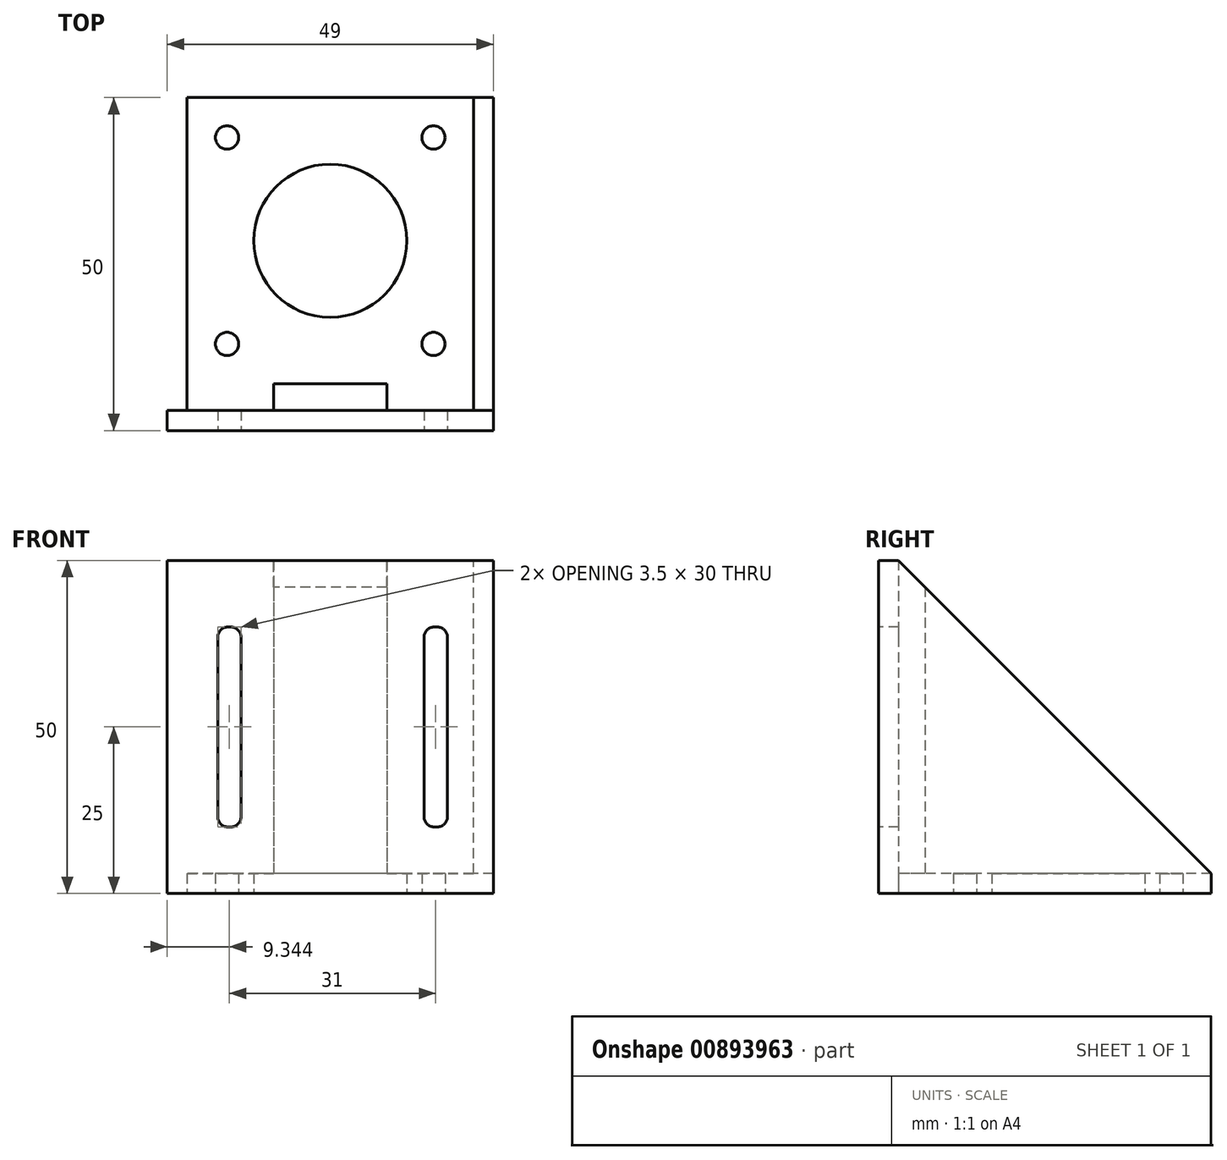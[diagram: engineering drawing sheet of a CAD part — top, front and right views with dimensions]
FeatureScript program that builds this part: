
annotation { "Feature Type Name" : "Feature", "Feature Type Description" : "" }
export const myFeature = defineFeature(function(context is Context, id is Id, definition is map)
    precondition{}
    {
        {
            var Q0;
            Q0=qCreatedBy(makeId("Top.planeOp"),FACE);
            var sketch = newSketch(context, id + "F0", { "sketchPlane" : qUnion([Q0])});
            skLineSegment(sketch, "E0.bottom", {"start": v(21.5, 21.5) * mm, "end": v(-21.5, 21.5) * mm});
            skLineSegment(sketch, "E0.top", {"start": v(21.5, -21.5) * mm, "end": v(-21.5, -21.5) * mm});
            skLineSegment(sketch, "E0.left", {"start": v(21.5, 21.5) * mm, "end": v(21.5, -21.5) * mm});
            skLineSegment(sketch, "E0.right", {"start": v(-21.5, 21.5) * mm, "end": v(-21.5, -21.5) * mm});
            skPoint(sketch, "E0.middle", {"position": v(0, 0) * mm});
            skCircle(sketch, "E1", {"center": v(0, 0) * mm, "radius": 11.5 * mm});
            skCircle(sketch, "E2", {"center": v(15.5, 15.5) * mm, "radius": 1.75 * mm});
            skCircle(sketch, "E3.0.1.0", {"center": v(15.5, -15.5) * mm, "radius": 1.75 * mm});
            skCircle(sketch, "E3.1.0.0", {"center": v(-15.5, 15.5) * mm, "radius": 1.75 * mm});
            skCircle(sketch, "E3.1.1.0", {"center": v(-15.5, -15.5) * mm, "radius": 1.75 * mm});
            skLineSegment(sketch, "E3.direction1", {"start": v(15.5, 15.5) * mm, "end": v(-15.5, 15.5) * mm, "construction": true});
            skLineSegment(sketch, "E3.direction2", {"start": v(15.5, 15.5) * mm, "end": v(15.5, -15.5) * mm, "construction": true});
            skLineSegment(sketch, "E4.top", {"start": v(-24.5, -28.5) * mm, "end": v(24.5, -28.5) * mm});
            skLineSegment(sketch, "E5.top", {"start": v(-24.5, -25.5) * mm, "end": v(24.5, -25.5) * mm});
            skLineSegment(sketch, "E5.left", {"start": v(-24.5, -28.5) * mm, "end": v(-24.5, -25.5) * mm});
            skLineSegment(sketch, "E5.right", {"start": v(24.5, -28.5) * mm, "end": v(24.5, -25.5) * mm});
            skLineSegment(sketch, "E6", {"start": v(-8.5, -21.5) * mm, "end": v(-8.5, -25.5) * mm});
            skLineSegment(sketch, "E7", {"start": v(8.5, -21.5) * mm, "end": v(8.5, -25.5) * mm});
            skLineSegment(sketch, "E8.bottom", {"start": v(-24.5, -25.5) * mm, "end": v(-21.5, -25.5) * mm});
            skLineSegment(sketch, "E8.top", {"start": v(-24.5, 21.5) * mm, "end": v(-21.5, 21.5) * mm});
            skLineSegment(sketch, "E8.left", {"start": v(-24.5, -25.5) * mm, "end": v(-24.5, 21.5) * mm});
            skLineSegment(sketch, "E8.right", {"start": v(-21.5, -25.5) * mm, "end": v(-21.5, 21.5) * mm});
            skLineSegment(sketch, "E9.bottom", {"start": v(21.5, 21.5) * mm, "end": v(24.5, 21.5) * mm});
            skLineSegment(sketch, "E9.top", {"start": v(21.5, -25.5) * mm, "end": v(24.5, -25.5) * mm});
            skLineSegment(sketch, "E9.left", {"start": v(21.5, 21.5) * mm, "end": v(21.5, -25.5) * mm});
            skLineSegment(sketch, "E9.right", {"start": v(24.5, 21.5) * mm, "end": v(24.5, -25.5) * mm});
            skSolve(sketch);
        }
        {
            var Q0;
            {var subQ2=sQuery(id+"F0.wireOp",EDGE,"E8.bottom");Q0=makeQuery(id+"F0.imprint","IMPRINT",FACE,{"disambiguationData":[TD([[makeQuery(id+"F0.imprint","IMPRINT",EDGE,{"derivedFrom":subQ2}),1.0]])]});}
            var Q1;
            Q1=makeQuery(id+"F0.imprint","IMPRINT",FACE,{"disambiguationData":[TD([[makeQuery(id+"F0.imprint","IMPRINT",EDGE,{"derivedFrom":sQuery(id+"F0.wireOp",EDGE,"E4.top")}),1.0]])]});
            var Q2;
            {var subQ3=sQuery(id+"F0.wireOp",EDGE,"E9.bottom");Q2=makeQuery(id+"F0.imprint","IMPRINT",FACE,{"disambiguationData":[TD([[makeQuery(id+"F0.imprint","IMPRINT",EDGE,{"derivedFrom":subQ3}),-1.0]])]});}
            var Q3;
            {var subQ0=sQuery(id+"F0.wireOp",EDGE,"E6");Q3=makeQuery(id+"F0.imprint","IMPRINT",FACE,{"disambiguationData":[TD([[makeQuery(id+"F0.imprint","IMPRINT",EDGE,{"derivedFrom":subQ0}),1.0]])]});}
            extrude(context, id + "F1", {"entities" : qUnion([Q0, Q1, Q2, Q3]), "depth" : 50 * mm, "offsetDistance" : 25 * mm});
        }
        {
            var Q0;
            {var subQ1=sQuery(id+"F0.wireOp",EDGE,"E0.bottom");Q0=makeQuery(id+"F0.imprint","IMPRINT",FACE,{"disambiguationData":[TD([[makeQuery(id+"F0.imprint","IMPRINT",EDGE,{"derivedFrom":subQ1}),1.0]])]});}
            var Q1;
            {var subQ3=sQuery(id+"F0.wireOp",EDGE,"E7");Q1=makeQuery(id+"F0.imprint","IMPRINT",FACE,{"disambiguationData":[TD([[makeQuery(id+"F0.imprint","IMPRINT",EDGE,{"derivedFrom":subQ3}),1.0]])]});}
            var Q2;
            {var subQ3=sQuery(id+"F0.wireOp",EDGE,"E6");Q2=makeQuery(id+"F0.imprint","IMPRINT",FACE,{"disambiguationData":[TD([[makeQuery(id+"F0.imprint","IMPRINT",EDGE,{"derivedFrom":subQ3}),-1.0]])]});}
            extrude(context, id + "F2", {"entities" : qUnion([Q0, Q1, Q2]), "operationType" : NewBodyOperationType.ADD, "depth" : 3 * mm, "offsetDistance" : 25 * mm});
        }
        {
            var Q0;
            Q0=makeQuery(id+"F1.opExtrude","SWEPT_FACE",FACE,{"disambiguationData":[OSD([sQuery(id+"F0.wireOp",EDGE,"E9.left")])]});
            var sketch = newSketch(context, id + "F3", { "sketchPlane" : qUnion([Q0])});
            skLineSegment(sketch, "E10", {"start": v(25.5, 50) * mm, "end": v(-21.5, 3) * mm});
            skLineSegment(sketch, "E11", {"start": v(-21.5, 3) * mm, "end": v(-21.5, 50) * mm});
            skLineSegment(sketch, "E12", {"start": v(-21.5, 50) * mm, "end": v(25.5, 50) * mm});
            skSolve(sketch);
        }
        {
            var Q0;
            Q0=makeQuery(id+"F3.imprint","IMPRINT",FACE,{"disambiguationData":[TD([[makeQuery(id+"F3.imprint","IMPRINT",EDGE,{"derivedFrom":sQuery(id+"F3.wireOp",EDGE,"E10")}),-1.0]])]});
            extrude(context, id + "F4", {"entities" : qUnion([Q0]), "operationType" : NewBodyOperationType.REMOVE, "oppositeDirection" : true, "depth" : 5 * mm, "offsetDistance" : 25 * mm, "hasSecondDirection" : true, "secondDirectionOppositeDirection" : false, "secondDirectionDepth" : 50 * mm});
        }
        {
            var Q0;
            Q0=makeQuery(id+"F1.opExtrude","SWEPT_FACE",FACE,{"disambiguationData":[OSD([sQuery(id+"F0.wireOp",EDGE,"E4.top")])]});
            var sketch = newSketch(context, id + "F5", { "sketchPlane" : qUnion([Q0])});
            skLineSegment(sketch, "E13.bottom", {"start": v(16.1, 40) * mm, "end": v(15.6, 40) * mm});
            skLineSegment(sketch, "E13.top", {"start": v(16.1, 10) * mm, "end": v(15.6, 10) * mm});
            skLineSegment(sketch, "E13.left", {"start": v(17.6, 38.5) * mm, "end": v(17.6, 11.5) * mm});
            skLineSegment(sketch, "E13.right", {"start": v(14.1, 38.5) * mm, "end": v(14.1, 11.5) * mm});
            skPoint(sketch, "E13.middle", {"position": v(15.84, 25) * mm});
            skPoint(sketch, "E14.visualSharp", {"position": v(17.6, 40) * mm});
            skArc(sketch, "E14.filletArc", {"start": v(17.6, 38.5) * mm, "mid": v(17.16, 39.56) * mm, "end": v(16.1, 40) * mm});
            skPoint(sketch, "E15.visualSharp", {"position": v(14.1, 40) * mm});
            skArc(sketch, "E15.filletArc", {"start": v(15.6, 40) * mm, "mid": v(14.53, 39.56) * mm, "end": v(14.1, 38.5) * mm});
            skPoint(sketch, "E16.visualSharp", {"position": v(14.1, 10) * mm});
            skArc(sketch, "E16.filletArc", {"start": v(14.1, 11.5) * mm, "mid": v(14.53, 10.44) * mm, "end": v(15.6, 10) * mm});
            skPoint(sketch, "E17.visualSharp", {"position": v(17.6, 10) * mm});
            skArc(sketch, "E17.filletArc", {"start": v(16.1, 10) * mm, "mid": v(17.16, 10.44) * mm, "end": v(17.6, 11.5) * mm});
            skLineSegment(sketch, "E18.1.0.0", {"start": v(-13.4, 38.5) * mm, "end": v(-13.4, 11.5) * mm});
            skPoint(sketch, "E18.1.0.1", {"position": v(-13.4, 40) * mm});
            skLineSegment(sketch, "E18.1.0.2", {"start": v(-16.9, 38.5) * mm, "end": v(-16.9, 11.5) * mm});
            skPoint(sketch, "E18.1.0.3", {"position": v(-15.16, 25) * mm});
            skPoint(sketch, "E18.1.0.4", {"position": v(-13.4, 10) * mm});
            skPoint(sketch, "E18.1.0.5", {"position": v(-16.9, 40) * mm});
            skPoint(sketch, "E18.1.0.6", {"position": v(-16.9, 10) * mm});
            skArc(sketch, "E18.1.0.7", {"start": v(-13.4, 38.5) * mm, "mid": v(-13.84, 39.56) * mm, "end": v(-14.9, 40) * mm});
            skArc(sketch, "E18.1.0.8", {"start": v(-16.9, 11.5) * mm, "mid": v(-16.47, 10.44) * mm, "end": v(-15.4, 10) * mm});
            skArc(sketch, "E18.1.0.9", {"start": v(-15.4, 40) * mm, "mid": v(-16.47, 39.56) * mm, "end": v(-16.9, 38.5) * mm});
            skArc(sketch, "E18.1.0.10", {"start": v(-14.9, 10) * mm, "mid": v(-13.84, 10.44) * mm, "end": v(-13.4, 11.5) * mm});
            skLineSegment(sketch, "E18.1.0.11", {"start": v(-14.9, 40) * mm, "end": v(-15.4, 40) * mm});
            skLineSegment(sketch, "E18.1.0.12", {"start": v(-14.9, 10) * mm, "end": v(-15.4, 10) * mm});
            skLineSegment(sketch, "E18.direction1", {"start": v(14.1, 10) * mm, "end": v(-16.9, 10) * mm, "construction": true});
            skSolve(sketch);
        }
        {
            var Q0;
            Q0=makeQuery(id+"F5.imprint","IMPRINT",FACE,{"disambiguationData":[TD([[makeQuery(id+"F5.imprint","IMPRINT",EDGE,{"derivedFrom":sQuery(id+"F5.wireOp",EDGE,"E13.bottom")}),1.0]])]});
            var Q1;
            Q1=makeQuery(id+"F5.imprint","IMPRINT",FACE,{"disambiguationData":[TD([[makeQuery(id+"F5.imprint","IMPRINT",EDGE,{"derivedFrom":sQuery(id+"F5.wireOp",EDGE,"E18.1.0.0")}),-1.0]])]});
            extrude(context, id + "F6", {"entities" : qUnion([Q0, Q1]), "operationType" : NewBodyOperationType.REMOVE, "oppositeDirection" : true, "depth" : 3 * mm, "offsetDistance" : 25 * mm});
        }
    });
